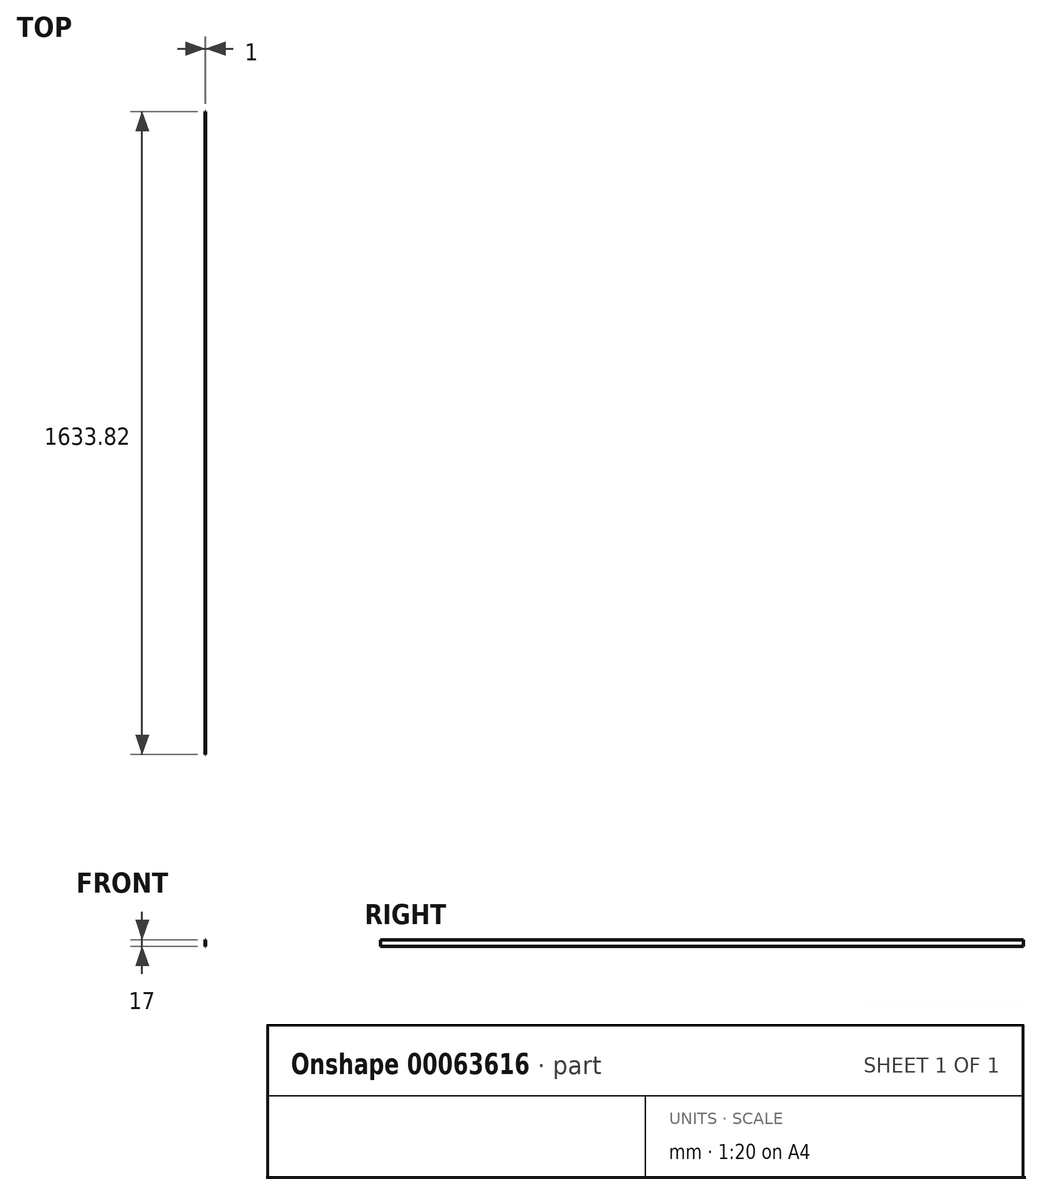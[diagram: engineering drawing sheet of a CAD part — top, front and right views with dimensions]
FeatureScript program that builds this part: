
annotation { "Feature Type Name" : "Feature", "Feature Type Description" : "" }
export const myFeature = defineFeature(function(context is Context, id is Id, definition is map)
    precondition{}
    {
        {
            var Q0;
            Q0=qCreatedBy(makeId("Right.planeOp"),FACE);
            var sketch = newSketch(context, id + "F0", { "sketchPlane" : qUnion([Q0])});
            skLineSegment(sketch, "E0.bottom", {"start": v(0, 0) * mm, "end": v(-1633.82, 0) * mm});
            skLineSegment(sketch, "E0.top", {"start": v(0, -17) * mm, "end": v(-1633.82, -17) * mm});
            skLineSegment(sketch, "E0.left", {"start": v(0, 0) * mm, "end": v(0, -17) * mm});
            skLineSegment(sketch, "E0.right", {"start": v(-1633.82, 0) * mm, "end": v(-1633.82, -17) * mm});
            skSolve(sketch);
        }
        {
            var Q0;
            Q0=makeQuery(id+"F0.imprint","IMPRINT",FACE,{"disambiguationData":[TD([[makeQuery(id+"F0.imprint","IMPRINT",EDGE,{"derivedFrom":sQuery(id+"F0.wireOp",EDGE,"E0.bottom")}),1.0]])]});
            extrude(context, id + "F1", {"entities" : qUnion([Q0]), "depth" : 1 * mm});
        }
    });
